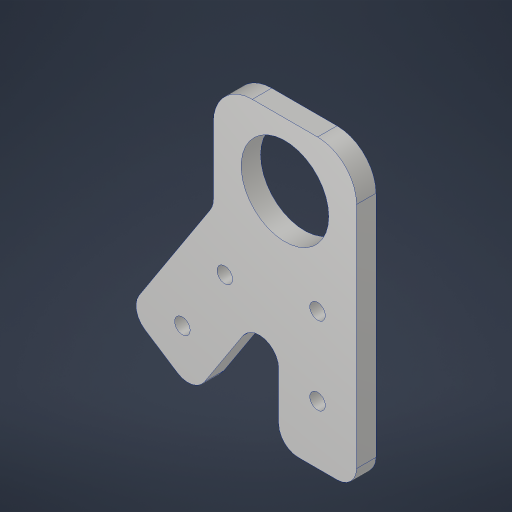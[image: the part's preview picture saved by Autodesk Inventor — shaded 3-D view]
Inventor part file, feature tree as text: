
AUTODESK INVENTOR PART (.ipt)
format: ipt  version: 2023.4 (Build 274418000, 418)  size: 246,784 bytes
history: native  units: in
note: dims shown in document units (in); Inventor stores cm internally (conversion verified against a paired STEP export)
features: projected_geometry x3, sketch x2, extrude x2, hole x2, fillet x2
ambient origin geometry x8: Origin, YZ Plane, XZ Plane, XY Plane, X Axis, Y Axis, Z Axis, Center Point
bodies: Solid1 (feature_tree)
feature tree (11):
  sketch  "Sketch1"  dims[d0=1.0in d1=1.0in]
  extrude  "Extrusion1"  Depth=1.0in
  hole  "Hole1"  [1 undecoded]
  sketch  "Sketch2"  dims[d2=0.2268in d3=2.0in d4=1.0in d5=0.5in d6=1.0in d7=0.5in d8=2.25in d9=0.25in d10=0.0in d11=0.201in d12=0.75in d13=0.385in d14=0.25in d15=0.5635in d16=1.0in d17=0.8108in d18=0.25in d19=1.125in d20=0.625in d21=0.25in d22=1.0in d23=0.0in d24=1.125in d25=0.75in d26=0.385in d27=0.25in d28=0.5635in d29=1.0in d30=0.8108in d31=0.5in]
  extrude  "Extrusion2"  Depth=1.0in
  hole  "Hole2"  [1 undecoded]
  fillet  "Fillet1"  Radius=1.0in
  fillet  "Fillet2"  Radius=0.5in
  projected_geometry  "Projected Loop1"
  projected_geometry  "Project Cut Edges1"
  projected_geometry  "Project Cut Edges2"
note: 2 required parameter values undecoded (feature->parameter linkage not recoverable at this tier; creation-order binding heuristic only, values carry confidence <= 0.55)
